# Revit family: SOFTYP003
name_source: partatom
category: Furniture
units: mm (PartAtom-declared; Revit-internal decimal feet)

## family parameters
Always vertical = Yes
Cut with Voids When Loaded = No
OmniClass Number = 23.40.20.00
OmniClass Title = General Furniture and Specialties
Render Appearance Source = Family Geometry
Room Calculation Point = No
Shared = No
Work Plane-Based = No

## types (1)
- SOFTYP003
    Cost = 13096 $
    Default Elevation = 0 mm  [stored 0 ft]
    Description = 1 x Soft Modular Lounge Corner, 45-degree, 1 x Soft Modular Lounge Corner, 90-degree, 1 x Soft Modular Lounge, 1 x Soft Modular Lounge, Single Arm LH, 1 x Soft Modular Lounge, Single Arm RH
    Exported From CET Designer = Yes
    Manufacturer = AIS
    Model = LSOFTCRNR45
    Show SOFTYP003 = Yes
    VisibilityIndex = 0

note: [stored X ft] marks values corroborated as IEEE doubles in the binary element streams (Revit-internal decimal feet)

## geometry (parser evidence)
native form markers: Sweep x3
no freeform markers — native parametric forms only
